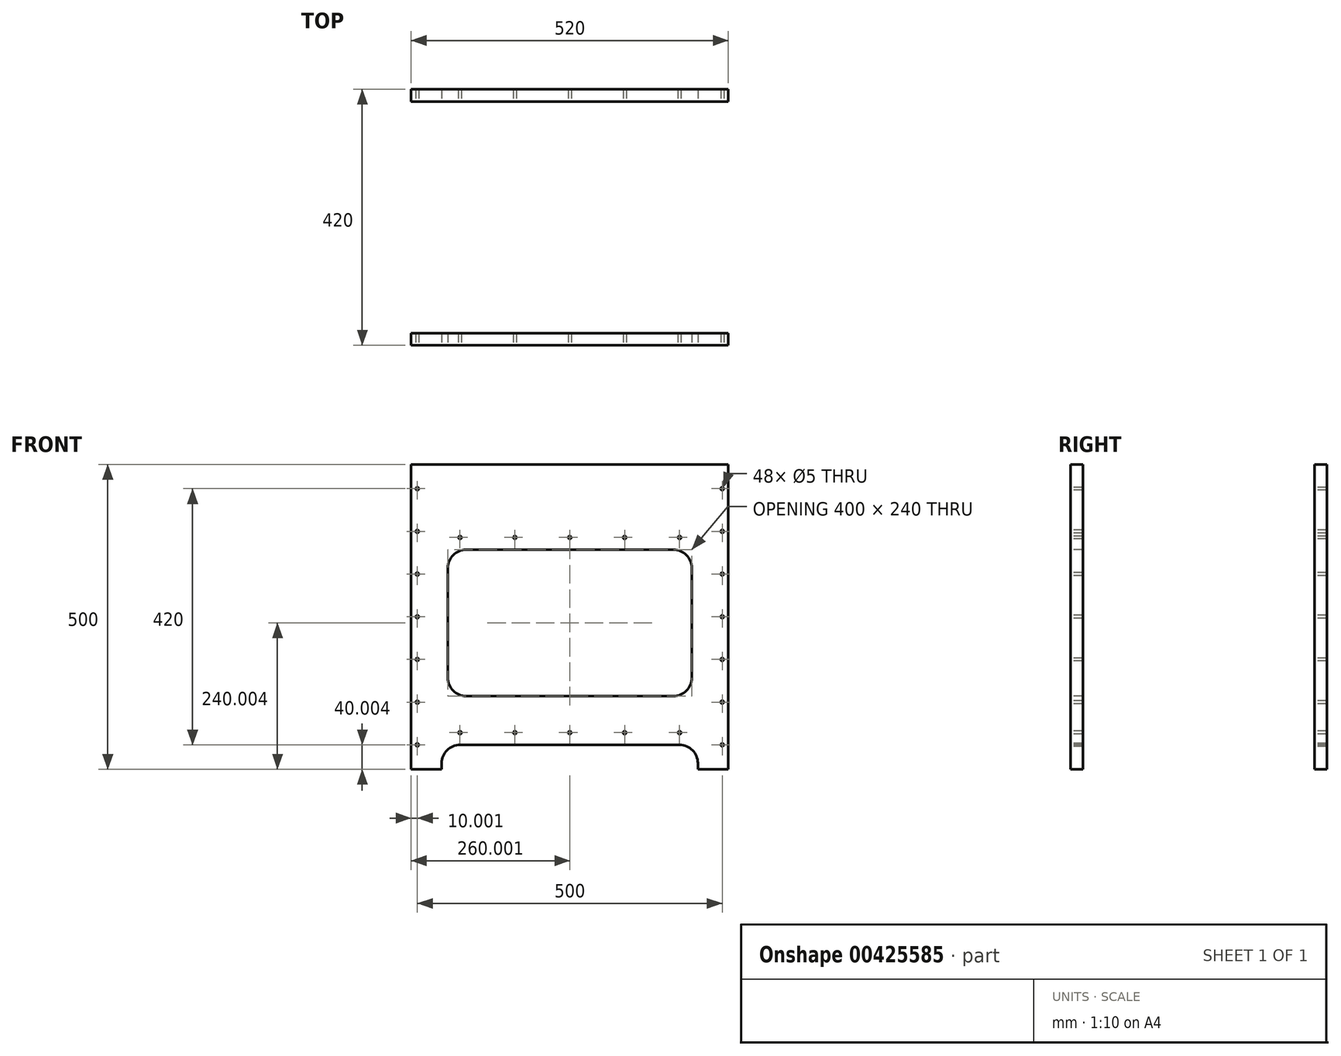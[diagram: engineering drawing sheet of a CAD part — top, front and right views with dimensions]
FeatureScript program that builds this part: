
annotation { "Feature Type Name" : "Feature", "Feature Type Description" : "" }
export const myFeature = defineFeature(function(context is Context, id is Id, definition is map)
    precondition{}
    {
        {
            var Q0;
            Q0=qCreatedBy(makeId("Front.planeOp"),FACE);
            var sketch = newSketch(context, id + "F0", { "sketchPlane" : qUnion([Q0])});
            skLineSegment(sketch, "E0.bottom", {"start": v(-236.46, 241.12) * mm, "end": v(283.54, 241.12) * mm});
            skLineSegment(sketch, "E0.top", {"start": v(-236.46, -258.88) * mm, "end": v(283.54, -258.88) * mm});
            skLineSegment(sketch, "E0.left", {"start": v(-236.46, 241.12) * mm, "end": v(-236.46, -258.88) * mm});
            skLineSegment(sketch, "E0.right", {"start": v(283.54, 241.12) * mm, "end": v(283.54, -258.88) * mm});
            skSolve(sketch);
        }
        {
            var Q0;
            Q0 = qSketchRegion(id + "F0", true);
            extrude(context, id + "F1", {"entities" : qUnion([Q0]), "depth" : 20 * mm});
        }
        {
            var Q0;
            Q0=makeQuery(id+"F1.opExtrude","CAP_FACE",FACE,{"disambiguationData":[OSD([sQuery(id+"F0.wireOp",EDGE,"E0.bottom"),sQuery(id+"F0.wireOp",EDGE,"E0.top"),sQuery(id+"F0.wireOp",EDGE,"E0.left"),sQuery(id+"F0.wireOp",EDGE,"E0.right")])],"isStart":false});
            var sketch = newSketch(context, id + "F2", { "sketchPlane" : qUnion([Q0])});
            skLineSegment(sketch, "E1.bottom", {"start": v(23.54, -258.88) * mm, "end": v(-186.46, -258.88) * mm});
            skLineSegment(sketch, "E1.top", {"start": v(23.54, -218.88) * mm, "end": v(-186.46, -218.88) * mm});
            skLineSegment(sketch, "E1.left", {"start": v(23.54, -258.88) * mm, "end": v(23.54, -218.88) * mm});
            skLineSegment(sketch, "E1.right", {"start": v(-186.46, -258.88) * mm, "end": v(-186.46, -218.88) * mm});
            skLineSegment(sketch, "E2.MirrorCS", {"start": v(-396.46, -218.88) * mm, "end": v(-186.46, -218.88) * mm});
            skLineSegment(sketch, "E3.MirrorCS", {"start": v(-396.46, -258.88) * mm, "end": v(-186.46, -258.88) * mm});
            skLineSegment(sketch, "E4.MirrorCS", {"start": v(233.54, -258.88) * mm, "end": v(233.54, -218.88) * mm});
            skLineSegment(sketch, "E5.MirrorCS", {"start": v(23.54, -218.88) * mm, "end": v(233.54, -218.88) * mm});
            skLineSegment(sketch, "E6.MirrorCS", {"start": v(23.54, -258.88) * mm, "end": v(233.54, -258.88) * mm});
            skSolve(sketch);
        }
        {
            var Q0;
            Q0 = qSketchRegion(id + "F2", true);
            extrude(context, id + "F3", {"entities" : qUnion([Q0]), "operationType" : NewBodyOperationType.REMOVE, "endBound" : BoundingType.UP_TO_NEXT, "oppositeDirection" : true, "depth" : 25 * mm});
        }
        {
            var Q0;
            Q0=makeQuery(id+"F3.boolean.opBoolean","COPY",EDGE,{"derivedFrom":makeQuery(id+"F3.opExtrude","SWEPT_EDGE",EDGE,{"disambiguationData":[OSD([sQuery(id+"F2.wireOp",EDGE,"E1.top"),sQuery(id+"F2.wireOp",EDGE,"E1.right"),sQuery(id+"F2.wireOp",EDGE,"E2.MirrorCS")])]})});
            var Q1;
            Q1=makeQuery(id+"F3.boolean.opBoolean","COPY",EDGE,{"derivedFrom":makeQuery(id+"F3.opExtrude","SWEPT_EDGE",EDGE,{"disambiguationData":[OSD([sQuery(id+"F2.wireOp",EDGE,"E4.MirrorCS"),sQuery(id+"F2.wireOp",EDGE,"E5.MirrorCS")])]})});
            fillet(context, id + "F4", {"entities" : qUnion([Q0, Q1]), "radius" : 30 * mm, "tangentPropagation" : true, "allowEdgeOverflow" : false});
        }
        {
            var Q0;
            Q0=makeQuery(id+"F1.opExtrude","SWEPT_BODY",BODY,{"disambiguationData":[OSD([sQuery(id+"F0.wireOp",EDGE,"E0.bottom"),sQuery(id+"F0.wireOp",EDGE,"E0.top"),sQuery(id+"F0.wireOp",EDGE,"E0.left"),sQuery(id+"F0.wireOp",EDGE,"E0.right")])]});
            transform(context, id + "F5", {"entities" : qUnion([Q0]), "transformType" : TransformType.TRANSLATION_3D, "dx" : 0 * mm, "dy" : 400 * mm, "dz" : 0 * mm, "makeCopy" : true});
        }
        {
            var Q0;
            Q0=makeQuery(id+"F1.opExtrude","CAP_FACE",FACE,{"disambiguationData":[OSD([sQuery(id+"F0.wireOp",EDGE,"E0.bottom"),sQuery(id+"F0.wireOp",EDGE,"E0.top"),sQuery(id+"F0.wireOp",EDGE,"E0.left"),sQuery(id+"F0.wireOp",EDGE,"E0.right")])],"isStart":false});
            var sketch = newSketch(context, id + "F6", { "sketchPlane" : qUnion([Q0])});
            skLineSegment(sketch, "E7.bottom", {"start": v(-176.46, 101.12) * mm, "end": v(23.54, 101.12) * mm});
            skLineSegment(sketch, "E7.top", {"start": v(-176.46, -138.88) * mm, "end": v(23.54, -138.88) * mm});
            skLineSegment(sketch, "E7.left", {"start": v(-176.46, 101.12) * mm, "end": v(-176.46, -138.88) * mm});
            skLineSegment(sketch, "E7.right", {"start": v(23.54, 101.12) * mm, "end": v(23.54, -138.88) * mm});
            skLineSegment(sketch, "E8", {"start": v(23.54, 241.12) * mm, "end": v(23.54, -218.88) * mm});
            skLineSegment(sketch, "E9.MirrorCS", {"start": v(223.54, 101.12) * mm, "end": v(23.54, 101.12) * mm});
            skLineSegment(sketch, "E10.MirrorCS", {"start": v(223.54, -138.88) * mm, "end": v(23.54, -138.88) * mm});
            skLineSegment(sketch, "E11.MirrorCS", {"start": v(223.54, 101.12) * mm, "end": v(223.54, -138.88) * mm});
            skSolve(sketch);
        }
        {
            var Q0;
            Q0 = qSketchRegion(id + "F6", true);
            extrude(context, id + "F7", {"entities" : qUnion([Q0]), "operationType" : NewBodyOperationType.REMOVE, "endBound" : BoundingType.UP_TO_NEXT, "oppositeDirection" : true, "depth" : 25 * mm});
        }
        {
            var Q0;
            Q0=makeQuery(id+"F7.boolean.opBoolean","COPY",EDGE,{"derivedFrom":makeQuery(id+"F7.opExtrude","SWEPT_EDGE",EDGE,{"disambiguationData":[OSD([sQuery(id+"F6.wireOp",EDGE,"E7.bottom"),sQuery(id+"F6.wireOp",EDGE,"E7.left")])]})});
            var Q1;
            Q1=makeQuery(id+"F7.boolean.opBoolean","COPY",EDGE,{"derivedFrom":makeQuery(id+"F7.opExtrude","SWEPT_EDGE",EDGE,{"disambiguationData":[OSD([sQuery(id+"F6.wireOp",EDGE,"E7.top"),sQuery(id+"F6.wireOp",EDGE,"E7.left")])]})});
            var Q2;
            Q2=makeQuery(id+"F7.boolean.opBoolean","COPY",EDGE,{"derivedFrom":makeQuery(id+"F7.opExtrude","SWEPT_EDGE",EDGE,{"disambiguationData":[OSD([sQuery(id+"F6.wireOp",EDGE,"E9.MirrorCS"),sQuery(id+"F6.wireOp",EDGE,"E11.MirrorCS")])]})});
            var Q3;
            Q3=makeQuery(id+"F7.boolean.opBoolean","COPY",EDGE,{"derivedFrom":makeQuery(id+"F7.opExtrude","SWEPT_EDGE",EDGE,{"disambiguationData":[OSD([sQuery(id+"F6.wireOp",EDGE,"E10.MirrorCS"),sQuery(id+"F6.wireOp",EDGE,"E11.MirrorCS")])]})});
            fillet(context, id + "F8", {"entities" : qUnion([Q0, Q1, Q2, Q3]), "radius" : 30 * mm, "tangentPropagation" : true, "allowEdgeOverflow" : false});
        }
        {
            var Q0;
            Q0=makeQuery(id+"F1.opExtrude","CAP_FACE",FACE,{"disambiguationData":[OSD([sQuery(id+"F0.wireOp",EDGE,"E0.bottom"),sQuery(id+"F0.wireOp",EDGE,"E0.top"),sQuery(id+"F0.wireOp",EDGE,"E0.left"),sQuery(id+"F0.wireOp",EDGE,"E0.right")])],"isStart":false});
            var sketch = newSketch(context, id + "F9", { "sketchPlane" : qUnion([Q0])});
            skPoint(sketch, "E12", {"position": v(-226.46, 61.12) * mm});
            skPoint(sketch, "E13", {"position": v(-226.46, -8.88) * mm});
            skPoint(sketch, "E14", {"position": v(-226.46, -78.88) * mm});
            skPoint(sketch, "E15", {"position": v(-226.46, -148.88) * mm});
            skPoint(sketch, "E16", {"position": v(-226.46, -218.88) * mm});
            skPoint(sketch, "E17", {"position": v(-226.46, 131.12) * mm});
            skPoint(sketch, "E18", {"position": v(-226.46, 201.12) * mm});
            skLineSegment(sketch, "E19", {"start": v(23.54, 241.12) * mm, "end": v(23.54, -218.88) * mm});
            skPoint(sketch, "E20.MirrorP", {"position": v(273.54, 201.12) * mm});
            skPoint(sketch, "E21.MirrorP", {"position": v(273.54, 131.12) * mm});
            skPoint(sketch, "E22.MirrorP", {"position": v(273.54, 61.12) * mm});
            skPoint(sketch, "E23.MirrorP", {"position": v(273.54, -8.88) * mm});
            skPoint(sketch, "E24.MirrorP", {"position": v(273.54, -78.88) * mm});
            skPoint(sketch, "E25.MirrorP", {"position": v(273.54, -148.88) * mm});
            skPoint(sketch, "E26.MirrorP", {"position": v(273.54, -218.88) * mm});
            skSolve(sketch);
        }
        {
            var Q0;
            Q0=sQuery(id+"F9.wireOp",VERTEX,"E18");
            var Q1;
            Q1=sQuery(id+"F9.wireOp",VERTEX,"E17");
            var Q2;
            Q2=sQuery(id+"F9.wireOp",VERTEX,"E12");
            var Q3;
            Q3=sQuery(id+"F9.wireOp",VERTEX,"E13");
            var Q4;
            Q4=sQuery(id+"F9.wireOp",VERTEX,"E14");
            var Q5;
            Q5=sQuery(id+"F9.wireOp",VERTEX,"E15");
            var Q6;
            Q6=sQuery(id+"F9.wireOp",VERTEX,"E26.MirrorP");
            var Q7;
            Q7=sQuery(id+"F9.wireOp",VERTEX,"E25.MirrorP");
            var Q8;
            Q8=sQuery(id+"F9.wireOp",VERTEX,"E24.MirrorP");
            var Q9;
            Q9=sQuery(id+"F9.wireOp",VERTEX,"E23.MirrorP");
            var Q10;
            Q10=sQuery(id+"F9.wireOp",VERTEX,"E22.MirrorP");
            var Q11;
            Q11=sQuery(id+"F9.wireOp",VERTEX,"E21.MirrorP");
            var Q12;
            Q12=sQuery(id+"F9.wireOp",VERTEX,"E20.MirrorP");
            var Q13;
            Q13=sQuery(id+"F9.wireOp",VERTEX,"E16");
            var Q14;
            Q14=makeQuery(id+"F1.opExtrude","SWEPT_BODY",BODY,{"disambiguationData":[OSD([sQuery(id+"F0.wireOp",EDGE,"E0.bottom"),sQuery(id+"F0.wireOp",EDGE,"E0.top"),sQuery(id+"F0.wireOp",EDGE,"E0.left"),sQuery(id+"F0.wireOp",EDGE,"E0.right")])]});
            var Q15;
            Q15=makeQuery(id+"F5.opPattern","COPY",BODY,{"derivedFrom":makeQuery(id+"F1.opExtrude","SWEPT_BODY",BODY,{"disambiguationData":[OSD([sQuery(id+"F0.wireOp",EDGE,"E0.bottom"),sQuery(id+"F0.wireOp",EDGE,"E0.top"),sQuery(id+"F0.wireOp",EDGE,"E0.left"),sQuery(id+"F0.wireOp",EDGE,"E0.right")])]}),"instanceName":"1"});
            hole(context, id + "F10", {"style" : HoleStyle.SIMPLE, "endStyle" : HoleEndStyle.THROUGH, "holeDiameter" : 5 * mm, "isTappedThrough" : true, "tappedDepth" : 12 * mm, "tapClearance" : 3, "locations" : qUnion([Q0, Q1, Q2, Q3, Q4, Q5, Q6, Q7, Q8, Q9, Q10, Q11, Q12, Q13]), "scope" : qUnion([Q14, Q15])});
        }
        {
            var Q0;
            Q0=makeQuery(id+"F1.opExtrude","CAP_FACE",FACE,{"disambiguationData":[OSD([sQuery(id+"F0.wireOp",EDGE,"E0.bottom"),sQuery(id+"F0.wireOp",EDGE,"E0.top"),sQuery(id+"F0.wireOp",EDGE,"E0.left"),sQuery(id+"F0.wireOp",EDGE,"E0.right")])],"isStart":false});
            var sketch = newSketch(context, id + "F11", { "sketchPlane" : qUnion([Q0])});
            skLineSegment(sketch, "E27", {"start": v(23.54, 241.12) * mm, "end": v(23.54, -218.88) * mm});
            skPoint(sketch, "E28", {"position": v(23.54, -198.88) * mm});
            skPoint(sketch, "E29", {"position": v(-66.46, -198.88) * mm});
            skPoint(sketch, "E30", {"position": v(-156.46, -198.88) * mm});
            skPoint(sketch, "E31", {"position": v(113.54, -198.88) * mm});
            skPoint(sketch, "E32", {"position": v(203.54, -198.88) * mm});
            skPoint(sketch, "E33", {"position": v(23.54, 121.12) * mm});
            skPoint(sketch, "E34", {"position": v(113.54, 121.12) * mm});
            skPoint(sketch, "E35", {"position": v(203.54, 121.12) * mm});
            skPoint(sketch, "E36", {"position": v(-66.46, 121.12) * mm});
            skPoint(sketch, "E37", {"position": v(-156.46, 121.12) * mm});
            skSolve(sketch);
        }
        {
            var Q0;
            Q0=sQuery(id+"F11.wireOp",VERTEX,"47aba270-c96d-4621-aca0-4de994665364");
            var Q1;
            Q1=sQuery(id+"F11.wireOp",VERTEX,"E37");
            var Q2;
            Q2=sQuery(id+"F11.wireOp",VERTEX,"E36");
            var Q3;
            Q3=sQuery(id+"F11.wireOp",VERTEX,"E33");
            var Q4;
            Q4=sQuery(id+"F11.wireOp",VERTEX,"E34");
            var Q5;
            Q5=sQuery(id+"F11.wireOp",VERTEX,"E35");
            var Q6;
            Q6=sQuery(id+"F11.wireOp",VERTEX,"7c7ab13b-cd3c-4d62-b251-0e5a6df15394");
            var Q7;
            Q7=sQuery(id+"F11.wireOp",VERTEX,"d6a641a7-1802-4a0c-9338-7a09e17d65d8");
            var Q8;
            Q8=sQuery(id+"F11.wireOp",VERTEX,"E32");
            var Q9;
            Q9=sQuery(id+"F11.wireOp",VERTEX,"E31");
            var Q10;
            Q10=sQuery(id+"F11.wireOp",VERTEX,"E28");
            var Q11;
            Q11=sQuery(id+"F11.wireOp",VERTEX,"E29");
            var Q12;
            Q12=sQuery(id+"F11.wireOp",VERTEX,"E30");
            var Q13;
            Q13=sQuery(id+"F11.wireOp",VERTEX,"5469a048-09d6-4183-af46-e420677b11df");
            var Q14;
            Q14=makeQuery(id+"F1.opExtrude","SWEPT_BODY",BODY,{"disambiguationData":[OSD([sQuery(id+"F0.wireOp",EDGE,"E0.bottom"),sQuery(id+"F0.wireOp",EDGE,"E0.top"),sQuery(id+"F0.wireOp",EDGE,"E0.left"),sQuery(id+"F0.wireOp",EDGE,"E0.right")])]});
            var Q15;
            Q15=makeQuery(id+"F5.opPattern","COPY",BODY,{"derivedFrom":makeQuery(id+"F1.opExtrude","SWEPT_BODY",BODY,{"disambiguationData":[OSD([sQuery(id+"F0.wireOp",EDGE,"E0.bottom"),sQuery(id+"F0.wireOp",EDGE,"E0.top"),sQuery(id+"F0.wireOp",EDGE,"E0.left"),sQuery(id+"F0.wireOp",EDGE,"E0.right")])]}),"instanceName":"1"});
            hole(context, id + "F12", {"style" : HoleStyle.SIMPLE, "endStyle" : HoleEndStyle.THROUGH, "holeDiameter" : 5 * mm, "isTappedThrough" : true, "tappedDepth" : 12 * mm, "tapClearance" : 3, "locations" : qUnion([Q0, Q1, Q2, Q3, Q4, Q5, Q6, Q7, Q8, Q9, Q10, Q11, Q12, Q13]), "scope" : qUnion([Q14, Q15])});
        }
    });
